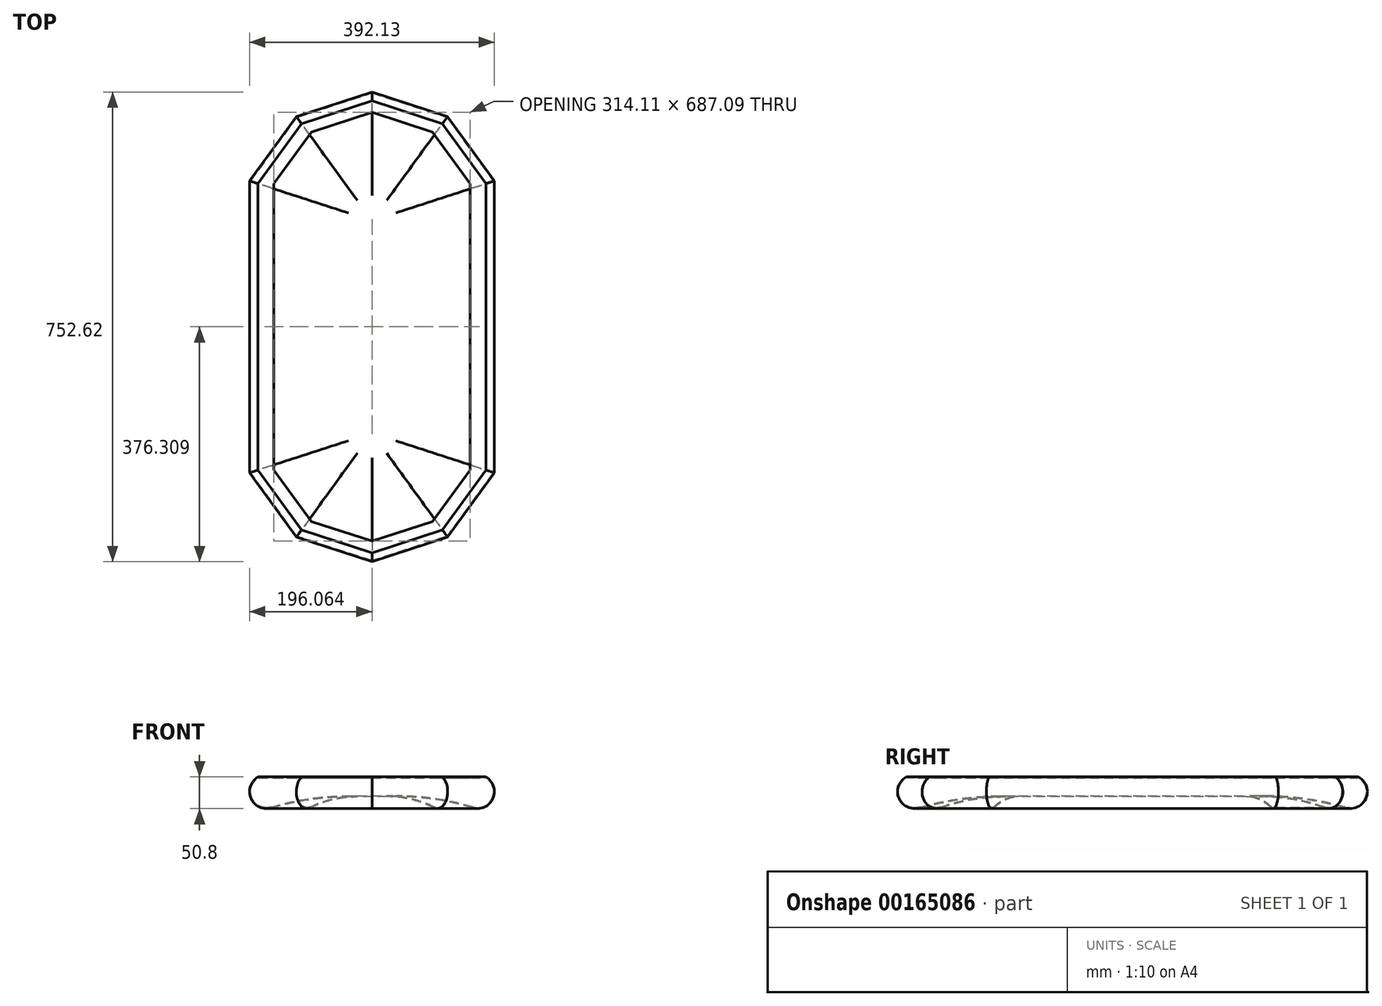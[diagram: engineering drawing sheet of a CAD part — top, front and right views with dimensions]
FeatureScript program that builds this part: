
annotation { "Feature Type Name" : "Feature", "Feature Type Description" : "" }
export const myFeature = defineFeature(function(context is Context, id is Id, definition is map)
    precondition{}
    {
        {
            var Q0;
            Q0=qCreatedBy(makeId("Top.planeOp"),FACE);
            var sketch = newSketch(context, id + "F0", { "sketchPlane" : qUnion([Q0])});
            skLineSegment(sketch, "E0.bottom", {"start": v(0, 59.28) * mm, "end": v(-364.91, 59.28) * mm, "construction": true});
            skLineSegment(sketch, "E0.top", {"start": v(0, 399.6) * mm, "end": v(-364.91, 399.6) * mm, "construction": true});
            skLineSegment(sketch, "E0.left", {"start": v(0, 399.6) * mm, "end": v(0, 59.28) * mm});
            skLineSegment(sketch, "E0.right", {"start": v(-364.91, 399.6) * mm, "end": v(-364.91, 59.28) * mm});
            skCircle(sketch, "E1.cCircle", {"center": v(-182.46, 59.28) * mm, "radius": 182.46 * mm, "construction": true});
            skLineSegment(sketch, "E1.0", {"start": v(-364.91, 0) * mm, "end": v(-364.91, 118.57) * mm});
            skLineSegment(sketch, "E1.1", {"start": v(-364.91, 118.57) * mm, "end": v(-295.22, 214.5) * mm, "construction": true});
            skLineSegment(sketch, "E1.2", {"start": v(-295.22, 214.5) * mm, "end": v(-182.46, 251.13) * mm, "construction": true});
            skLineSegment(sketch, "E1.3", {"start": v(-182.46, 251.13) * mm, "end": v(-69.7, 214.5) * mm, "construction": true});
            skLineSegment(sketch, "E1.4", {"start": v(-69.7, 214.5) * mm, "end": v(0, 118.57) * mm, "construction": true});
            skLineSegment(sketch, "E1.5", {"start": v(0, 118.57) * mm, "end": v(0, 0) * mm});
            skLineSegment(sketch, "E1.6", {"start": v(0, 0) * mm, "end": v(-69.7, -95.92) * mm});
            skLineSegment(sketch, "E1.7", {"start": v(-69.7, -95.92) * mm, "end": v(-182.46, -132.56) * mm});
            skLineSegment(sketch, "E1.8", {"start": v(-182.46, -132.56) * mm, "end": v(-295.22, -95.92) * mm});
            skLineSegment(sketch, "E1.9", {"start": v(-295.22, -95.92) * mm, "end": v(-364.91, 0) * mm});
            skPoint(sketch, "E1.0.midPoint", {"position": v(-364.91, 59.28) * mm});
            skCircle(sketch, "E2.cCircle", {"center": v(-182.46, 399.6) * mm, "radius": 182.46 * mm, "construction": true});
            skLineSegment(sketch, "E2.0", {"start": v(-364.91, 340.31) * mm, "end": v(-364.91, 458.88) * mm});
            skLineSegment(sketch, "E2.1", {"start": v(-364.91, 458.88) * mm, "end": v(-295.22, 554.8) * mm});
            skLineSegment(sketch, "E2.2", {"start": v(-295.22, 554.8) * mm, "end": v(-182.46, 591.44) * mm});
            skLineSegment(sketch, "E2.3", {"start": v(-182.46, 591.44) * mm, "end": v(-69.7, 554.8) * mm});
            skLineSegment(sketch, "E2.4", {"start": v(-69.7, 554.8) * mm, "end": v(0, 458.88) * mm});
            skLineSegment(sketch, "E2.5", {"start": v(0, 458.88) * mm, "end": v(0, 340.31) * mm});
            skLineSegment(sketch, "E2.6", {"start": v(0, 340.31) * mm, "end": v(-69.7, 244.39) * mm, "construction": true});
            skLineSegment(sketch, "E2.7", {"start": v(-69.7, 244.39) * mm, "end": v(-182.46, 207.75) * mm, "construction": true});
            skLineSegment(sketch, "E2.8", {"start": v(-182.46, 207.75) * mm, "end": v(-295.22, 244.39) * mm, "construction": true});
            skLineSegment(sketch, "E2.9", {"start": v(-295.22, 244.39) * mm, "end": v(-364.91, 340.31) * mm, "construction": true});
            skPoint(sketch, "E2.0.midPoint", {"position": v(-364.91, 399.6) * mm});
            skSolve(sketch);
        }
        {
            var Q0;
            Q0=qSketchRegion(id+"F0",true);
            extrude(context, id + "F1", {"entities" : qUnion([Q0]), "depth" : 1.59 * mm});
        }
        {
            var Q0;
            Q0=qCreatedBy(makeId("Front.planeOp"),FACE);
            var sketch = newSketch(context, id + "F2", { "sketchPlane" : qUnion([Q0])});
            skArc(sketch, "E3", {"start": v(-364.91, 1.59) * mm, "mid": v(-376.3, -32.75) * mm, "end": v(-343.53, -48.08) * mm});
            skLineSegment(sketch, "E4", {"start": v(-351.3, -21.99) * mm, "end": v(-343.99, -46.56) * mm, "construction": true});
            skLineSegment(sketch, "E5", {"start": v(-343.99, -46.56) * mm, "end": v(-343.53, -48.08) * mm, "construction": true});
            skArc(sketch, "E6", {"start": v(-364.48, 0) * mm, "mid": v(-374.76, -32.32) * mm, "end": v(-343.99, -46.56) * mm});
            skLineSegment(sketch, "E7", {"start": v(-182.46, 0) * mm, "end": v(-182.46, -28.58) * mm, "construction": true});
            skLineSegment(sketch, "E8.bottom", {"start": v(-182.46, -28.57) * mm, "end": v(-220.56, -28.57) * mm});
            skLineSegment(sketch, "E8.top", {"start": v(-182.46, -30.16) * mm, "end": v(-220.56, -30.16) * mm});
            skLineSegment(sketch, "E8.left", {"start": v(-182.46, -28.58) * mm, "end": v(-182.46, -30.16) * mm});
            skLineSegment(sketch, "E8.right", {"start": v(-220.56, -28.57) * mm, "end": v(-220.56, -30.16) * mm, "construction": true});
            skArc(sketch, "E9", {"start": v(-220.56, -28.58) * mm, "mid": v(-282.92, -33.1) * mm, "end": v(-343.99, -46.56) * mm});
            skArc(sketch, "E10", {"start": v(-220.56, -30.16) * mm, "mid": v(-282.7, -34.67) * mm, "end": v(-343.53, -48.08) * mm});
            skLineSegment(sketch, "E11", {"start": v(-182.46, -30.16) * mm, "end": v(-182.46, -49.21) * mm, "construction": true});
            skLineSegment(sketch, "E12", {"start": v(-182.46, -49.21) * mm, "end": v(-351.3, -49.21) * mm, "construction": true});
            skLineSegment(sketch, "E13.top", {"start": v(-364.91, 0) * mm, "end": v(-364.48, 0) * mm});
            skLineSegment(sketch, "E13.left", {"start": v(-364.91, 1.59) * mm, "end": v(-364.91, 0) * mm});
            skLineSegment(sketch, "E14.bottom", {"start": v(-364.91, 1.59) * mm, "end": v(-339.51, 1.59) * mm, "construction": true});
            skLineSegment(sketch, "E14.top", {"start": v(-364.91, 16.25) * mm, "end": v(-339.51, 16.25) * mm, "construction": true});
            skLineSegment(sketch, "E14.left", {"start": v(-364.91, 1.59) * mm, "end": v(-364.91, 16.25) * mm, "construction": true});
            skLineSegment(sketch, "E14.right", {"start": v(-339.51, 1.59) * mm, "end": v(-339.51, 16.25) * mm, "construction": true});
            skLineSegment(sketch, "E15", {"start": v(-364.91, 1.59) * mm, "end": v(-339.51, 16.25) * mm, "construction": true});
            skSolve(sketch);
        }
        {
            var Q0;
            Q0=makeQuery(id+"F2.imprint","IMPRINT",FACE,{"disambiguationData":[TD([[makeQuery(id+"F2.imprint","IMPRINT",EDGE,{"derivedFrom":sQuery(id+"F2.wireOp",EDGE,"E3")}),1.0]])]});
            var Q1;
            Q1=makeQuery(id+"F1.opExtrude","CAP_EDGE",EDGE,{"disambiguationData":[OSD([sQuery(id+"F0.wireOp",EDGE,"E0.right"),sQuery(id+"F0.wireOp",EDGE,"E1.0"),sQuery(id+"F0.wireOp",EDGE,"E2.0")])],"isStart":true});
            var Q2;
            Q2=makeQuery(id+"F1.opExtrude","CAP_EDGE",EDGE,{"disambiguationData":[OSD([sQuery(id+"F0.wireOp",EDGE,"E2.1")])],"isStart":true});
            var Q3;
            Q3=makeQuery(id+"F1.opExtrude","CAP_EDGE",EDGE,{"disambiguationData":[OSD([sQuery(id+"F0.wireOp",EDGE,"E2.2")])],"isStart":true});
            var Q4;
            Q4=makeQuery(id+"F1.opExtrude","CAP_EDGE",EDGE,{"disambiguationData":[OSD([sQuery(id+"F0.wireOp",EDGE,"E2.3")])],"isStart":true});
            var Q5;
            Q5=makeQuery(id+"F1.opExtrude","CAP_EDGE",EDGE,{"disambiguationData":[OSD([sQuery(id+"F0.wireOp",EDGE,"E2.4")])],"isStart":true});
            var Q6;
            Q6=makeQuery(id+"F1.opExtrude","CAP_EDGE",EDGE,{"disambiguationData":[OSD([sQuery(id+"F0.wireOp",EDGE,"E0.left"),sQuery(id+"F0.wireOp",EDGE,"E1.5"),sQuery(id+"F0.wireOp",EDGE,"E2.5")])],"isStart":true});
            sweep(context, id + "F3", {"operationType" : NewBodyOperationType.ADD, "profiles" : qUnion([Q0]), "path" : qUnion([Q1, Q2, Q3, Q4, Q5, Q6])});
        }
        {
            var Q0;
            Q0=makeQuery(id+"F1.opExtrude","CAP_FACE",FACE,{"disambiguationData":[OSD([sQuery(id+"F0.wireOp",EDGE,"E0.left"),sQuery(id+"F0.wireOp",EDGE,"E0.right"),sQuery(id+"F0.wireOp",EDGE,"E1.0"),sQuery(id+"F0.wireOp",EDGE,"E1.5"),sQuery(id+"F0.wireOp",EDGE,"E1.6"),sQuery(id+"F0.wireOp",EDGE,"E1.7"),sQuery(id+"F0.wireOp",EDGE,"E1.8"),sQuery(id+"F0.wireOp",EDGE,"E1.9"),sQuery(id+"F0.wireOp",EDGE,"E2.0"),sQuery(id+"F0.wireOp",EDGE,"E2.1"),sQuery(id+"F0.wireOp",EDGE,"E2.2"),sQuery(id+"F0.wireOp",EDGE,"E2.3"),sQuery(id+"F0.wireOp",EDGE,"E2.4"),sQuery(id+"F0.wireOp",EDGE,"E2.5")])],"isStart":false});
            var sketch = newSketch(context, id + "F4", { "sketchPlane" : qUnion([Q0])});
            skLineSegment(sketch, "E16.bottom", {"start": v(325.54, -132.56) * mm, "end": v(-690.46, -132.56) * mm});
            skLineSegment(sketch, "E16.top", {"start": v(325.54, 229.44) * mm, "end": v(-690.46, 229.44) * mm});
            skLineSegment(sketch, "E16.left", {"start": v(325.54, -132.56) * mm, "end": v(325.54, 229.44) * mm});
            skLineSegment(sketch, "E16.right", {"start": v(-690.46, -132.56) * mm, "end": v(-690.46, 229.44) * mm});
            skLineSegment(sketch, "E17", {"start": v(-182.46, 591.44) * mm, "end": v(-182.46, 229.44) * mm, "construction": true});
            skSolve(sketch);
        }
        {
            var Q0;
            Q0 = qSketchRegion(id + "F4", true);
            extrude(context, id + "F5", {"entities" : qUnion([Q0]), "operationType" : NewBodyOperationType.REMOVE, "endBound" : BoundingType.THROUGH_ALL, "oppositeDirection" : true, "depth" : 25.4 * mm});
        }
        {
            var Q0;
            Q0=makeQuery(id+"F1.opExtrude","CAP_FACE",FACE,{"disambiguationData":[OSD([sQuery(id+"F0.wireOp",EDGE,"E0.left"),sQuery(id+"F0.wireOp",EDGE,"E0.right"),sQuery(id+"F0.wireOp",EDGE,"E1.0"),sQuery(id+"F0.wireOp",EDGE,"E1.5"),sQuery(id+"F0.wireOp",EDGE,"E1.6"),sQuery(id+"F0.wireOp",EDGE,"E1.7"),sQuery(id+"F0.wireOp",EDGE,"E1.8"),sQuery(id+"F0.wireOp",EDGE,"E1.9"),sQuery(id+"F0.wireOp",EDGE,"E2.0"),sQuery(id+"F0.wireOp",EDGE,"E2.1"),sQuery(id+"F0.wireOp",EDGE,"E2.2"),sQuery(id+"F0.wireOp",EDGE,"E2.3"),sQuery(id+"F0.wireOp",EDGE,"E2.4"),sQuery(id+"F0.wireOp",EDGE,"E2.5")])],"isStart":false});
            var sketch = newSketch(context, id + "F6", { "sketchPlane" : qUnion([Q0])});
            skCircle(sketch, "E18", {"center": v(-182.46, 229.44) * mm, "radius": 25.4 * mm});
            skSolve(sketch);
        }
        {
            var Q0;
            Q0=makeQuery(id+"F1.opExtrude","SWEPT_BODY",BODY,{"disambiguationData":[OSD([sQuery(id+"F0.wireOp",EDGE,"E0.left"),sQuery(id+"F0.wireOp",EDGE,"E0.right"),sQuery(id+"F0.wireOp",EDGE,"E1.0"),sQuery(id+"F0.wireOp",EDGE,"E1.5"),sQuery(id+"F0.wireOp",EDGE,"E1.6"),sQuery(id+"F0.wireOp",EDGE,"E1.7"),sQuery(id+"F0.wireOp",EDGE,"E1.8"),sQuery(id+"F0.wireOp",EDGE,"E1.9"),sQuery(id+"F0.wireOp",EDGE,"E2.0"),sQuery(id+"F0.wireOp",EDGE,"E2.1"),sQuery(id+"F0.wireOp",EDGE,"E2.2"),sQuery(id+"F0.wireOp",EDGE,"E2.3"),sQuery(id+"F0.wireOp",EDGE,"E2.4"),sQuery(id+"F0.wireOp",EDGE,"E2.5")])]});
            var Q1;
            Q1=sQuery(id+"F6.wireOp",EDGE,"E18");
            circularPattern(context, id + "F7", {"entities" : qUnion([Q0]), "axis" : qUnion([Q1]), "angle" : 180 * degree, "instanceCount" : 2});
        }
        {
            var Q0;
            Q0=makeQuery(id+"F7.opPattern","COPY",FACE,{"derivedFrom":makeQuery(id+"F1.opExtrude","CAP_FACE",FACE,{"disambiguationData":[OSD([sQuery(id+"F0.wireOp",EDGE,"E0.left"),sQuery(id+"F0.wireOp",EDGE,"E0.right"),sQuery(id+"F0.wireOp",EDGE,"E1.0"),sQuery(id+"F0.wireOp",EDGE,"E1.5"),sQuery(id+"F0.wireOp",EDGE,"E1.6"),sQuery(id+"F0.wireOp",EDGE,"E1.7"),sQuery(id+"F0.wireOp",EDGE,"E1.8"),sQuery(id+"F0.wireOp",EDGE,"E1.9"),sQuery(id+"F0.wireOp",EDGE,"E2.0"),sQuery(id+"F0.wireOp",EDGE,"E2.1"),sQuery(id+"F0.wireOp",EDGE,"E2.2"),sQuery(id+"F0.wireOp",EDGE,"E2.3"),sQuery(id+"F0.wireOp",EDGE,"E2.4"),sQuery(id+"F0.wireOp",EDGE,"E2.5")])],"isStart":false}),"instanceName":"1"});
            var sketch = newSketch(context, id + "F8", { "sketchPlane" : qUnion([Q0])});
            skLineSegment(sketch, "E19.bottom", {"start": v(-364.91, 114.72) * mm, "end": v(0, 114.72) * mm});
            skLineSegment(sketch, "E19.top", {"start": v(-364.91, 344.16) * mm, "end": v(0, 344.16) * mm});
            skLineSegment(sketch, "E19.left", {"start": v(-364.91, 114.72) * mm, "end": v(-364.91, 344.16) * mm});
            skLineSegment(sketch, "E19.right", {"start": v(0, 114.72) * mm, "end": v(0, 344.16) * mm});
            skSolve(sketch);
        }
        {
            var Q0;
            Q0 = qSketchRegion(id + "F8", true);
            extrude(context, id + "F9", {"entities" : qUnion([Q0]), "operationType" : NewBodyOperationType.ADD, "oppositeDirection" : true, "depth" : 1.59 * mm});
        }
        {
            var Q0;
            {var subQ0=makeQuery(id+"F1.opExtrude","CAP_FACE",FACE,{"disambiguationData":[OSD([sQuery(id+"F0.wireOp",EDGE,"E0.left"),sQuery(id+"F0.wireOp",EDGE,"E0.right"),sQuery(id+"F0.wireOp",EDGE,"E1.0"),sQuery(id+"F0.wireOp",EDGE,"E1.5"),sQuery(id+"F0.wireOp",EDGE,"E1.6"),sQuery(id+"F0.wireOp",EDGE,"E1.7"),sQuery(id+"F0.wireOp",EDGE,"E1.8"),sQuery(id+"F0.wireOp",EDGE,"E1.9"),sQuery(id+"F0.wireOp",EDGE,"E2.0"),sQuery(id+"F0.wireOp",EDGE,"E2.1"),sQuery(id+"F0.wireOp",EDGE,"E2.2"),sQuery(id+"F0.wireOp",EDGE,"E2.3"),sQuery(id+"F0.wireOp",EDGE,"E2.4"),sQuery(id+"F0.wireOp",EDGE,"E2.5")])],"isStart":false});Q0=makeQuery(id+"F9.boolean.opBoolean","MERGE",FACE,{"derivedFrom":[subQ0,makeQuery(id+"F7.opPattern","COPY",FACE,{"derivedFrom":subQ0,"instanceName":"1"}),makeQuery(id+"F9.opExtrude","CAP_FACE",FACE,{"disambiguationData":[OSD([sQuery(id+"F8.wireOp",EDGE,"E19.bottom"),sQuery(id+"F8.wireOp",EDGE,"E19.top"),sQuery(id+"F8.wireOp",EDGE,"E19.left"),sQuery(id+"F8.wireOp",EDGE,"E19.right")])],"isStart":true})]});}
            var sketch = newSketch(context, id + "F10", { "sketchPlane" : qUnion([Q0])});
            skLineSegment(sketch, "E20.bottom", {"start": v(-25.4, 51.03) * mm, "end": v(-339.51, 51.03) * mm, "construction": true});
            skLineSegment(sketch, "E20.top", {"start": v(-25.4, 407.85) * mm, "end": v(-339.51, 407.85) * mm, "construction": true});
            skLineSegment(sketch, "E20.left", {"start": v(-25.4, 51.03) * mm, "end": v(-25.4, 407.85) * mm});
            skLineSegment(sketch, "E20.right", {"start": v(-339.51, 51.03) * mm, "end": v(-339.51, 407.85) * mm});
            skCircle(sketch, "E21.cCircle", {"center": v(-182.46, 51.03) * mm, "radius": 157.06 * mm, "construction": true});
            skLineSegment(sketch, "E21.0", {"start": v(-85.4, -82.57) * mm, "end": v(-182.46, -114.1) * mm});
            skLineSegment(sketch, "E21.1", {"start": v(-182.46, -114.1) * mm, "end": v(-279.52, -82.57) * mm});
            skLineSegment(sketch, "E21.2", {"start": v(-279.52, -82.57) * mm, "end": v(-339.51, 0) * mm});
            skLineSegment(sketch, "E21.3", {"start": v(-339.51, 0) * mm, "end": v(-339.51, 102.06) * mm});
            skLineSegment(sketch, "E21.4", {"start": v(-339.51, 102.06) * mm, "end": v(-279.52, 184.63) * mm, "construction": true});
            skLineSegment(sketch, "E21.5", {"start": v(-279.52, 184.63) * mm, "end": v(-182.46, 216.17) * mm, "construction": true});
            skLineSegment(sketch, "E21.6", {"start": v(-182.46, 216.17) * mm, "end": v(-85.4, 184.63) * mm, "construction": true});
            skLineSegment(sketch, "E21.7", {"start": v(-85.4, 184.63) * mm, "end": v(-25.4, 102.06) * mm, "construction": true});
            skLineSegment(sketch, "E21.8", {"start": v(-25.4, 102.06) * mm, "end": v(-25.4, 0) * mm});
            skLineSegment(sketch, "E21.9", {"start": v(-25.4, 0) * mm, "end": v(-85.4, -82.57) * mm});
            skPoint(sketch, "E21.0.midPoint", {"position": v(-133.92, -98.34) * mm});
            skLineSegment(sketch, "E22", {"start": v(-25.4, 0) * mm, "end": v(0, 0) * mm, "construction": true});
            skLineSegment(sketch, "E23", {"start": v(-25.4, 0) * mm, "end": v(-339.51, 0) * mm, "construction": true});
            skLineSegment(sketch, "E24", {"start": v(-339.51, 0) * mm, "end": v(-364.91, 0) * mm, "construction": true});
            skLineSegment(sketch, "E25", {"start": v(0, 458.88) * mm, "end": v(-25.4, 458.88) * mm, "construction": true});
            skLineSegment(sketch, "E26", {"start": v(-25.4, 458.88) * mm, "end": v(-339.51, 458.88) * mm, "construction": true});
            skLineSegment(sketch, "E27", {"start": v(-339.51, 458.88) * mm, "end": v(-364.91, 458.88) * mm, "construction": true});
            skCircle(sketch, "E28.cCircle", {"center": v(-182.46, 407.85) * mm, "radius": 157.06 * mm, "construction": true});
            skLineSegment(sketch, "E28.0", {"start": v(-182.46, 572.99) * mm, "end": v(-85.4, 541.45) * mm});
            skLineSegment(sketch, "E28.1", {"start": v(-85.4, 541.45) * mm, "end": v(-25.4, 458.88) * mm});
            skLineSegment(sketch, "E28.2", {"start": v(-25.4, 458.88) * mm, "end": v(-25.4, 356.82) * mm});
            skLineSegment(sketch, "E28.3", {"start": v(-25.4, 356.82) * mm, "end": v(-85.4, 274.25) * mm, "construction": true});
            skLineSegment(sketch, "E28.4", {"start": v(-85.4, 274.25) * mm, "end": v(-182.46, 242.7) * mm, "construction": true});
            skLineSegment(sketch, "E28.5", {"start": v(-182.46, 242.7) * mm, "end": v(-279.52, 274.25) * mm, "construction": true});
            skLineSegment(sketch, "E28.6", {"start": v(-279.52, 274.25) * mm, "end": v(-339.51, 356.82) * mm, "construction": true});
            skLineSegment(sketch, "E28.7", {"start": v(-339.51, 356.82) * mm, "end": v(-339.51, 458.88) * mm});
            skLineSegment(sketch, "E28.8", {"start": v(-339.51, 458.88) * mm, "end": v(-279.52, 541.45) * mm});
            skLineSegment(sketch, "E28.9", {"start": v(-279.52, 541.45) * mm, "end": v(-182.46, 572.99) * mm});
            skPoint(sketch, "E28.0.midPoint", {"position": v(-133.92, 557.22) * mm});
            skSolve(sketch);
        }
        {
            var Q0;
            Q0 = qSketchRegion(id + "F10", true);
            extrude(context, id + "F11", {"entities" : qUnion([Q0]), "operationType" : NewBodyOperationType.REMOVE, "oppositeDirection" : true, "depth" : 1.59 * mm});
        }
    });
